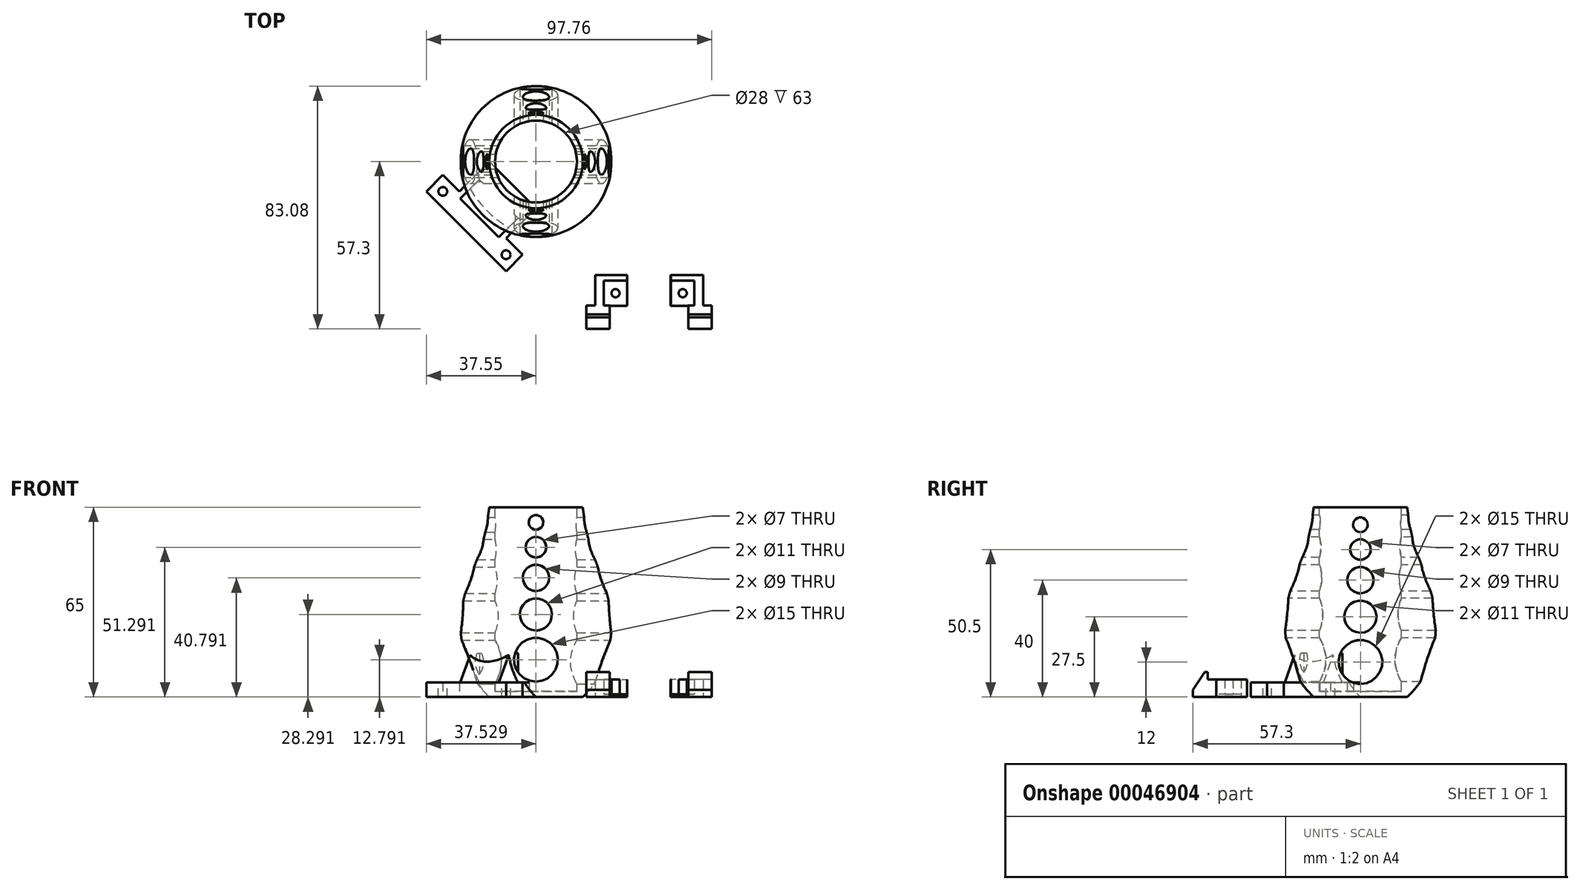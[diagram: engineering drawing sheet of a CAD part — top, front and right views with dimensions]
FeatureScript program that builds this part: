
annotation { "Feature Type Name" : "Feature", "Feature Type Description" : "" }
export const myFeature = defineFeature(function(context is Context, id is Id, definition is map)
    precondition{}
    {
        {
            var Q0;
            Q0=qCreatedBy(makeId("Front.planeOp"),FACE);
            var sketch = newSketch(context, id + "F0", { "sketchPlane" : qUnion([Q0])});
            skLineSegment(sketch, "E0", {"start": v(0, 0) * mm, "end": v(-16, 0) * mm});
            skLineSegment(sketch, "E1", {"start": v(0, 0) * mm, "end": v(0, 65) * mm, "construction": true});
            skLineSegment(sketch, "E2", {"start": v(0, 65) * mm, "end": v(-16, 65) * mm, "construction": true});
            skFitSpline(sketch, "E3", {"points": [v(-16, 0) * mm, v(-21.83, 7.5) * mm, v(-25.67, 28.22) * mm, v(-18.76, 51.24) * mm, v(-16, 65) * mm], "startDerivative": vector(-32.37, 32.77) * mm, "endDerivative": vector(7.4, 56.5) * mm});
            skLineSegment(sketch, "E4", {"start": v(-16, 65) * mm, "end": v(0, 65) * mm});
            skLineSegment(sketch, "E5", {"start": v(0, 65) * mm, "end": v(0, 0) * mm});
            skSolve(sketch);
        }
        {
            var Q0;
            Q0 = qSketchRegion(id + "F0", true);
            var Q1;
            Q1=sQuery(id+"F0.wireOp",EDGE,"E5");
            revolve(context, id + "F1", {"entities" : qUnion([Q0]), "axis" : qUnion([Q1]), "revolveType" : RevolveType.FULL});
        }
        {
            var Q0;
            Q0=makeQuery(id+"F1.opRevolve","SWEPT_FACE",FACE,{"disambiguationData":[OSD([sQuery(id+"F0.wireOp",EDGE,"E4")])]});
            var sketch = newSketch(context, id + "F2", { "sketchPlane" : qUnion([Q0])});
            skCircle(sketch, "E6", {"center": v(0, 0) * mm, "radius": 14 * mm});
            skCircle(sketch, "E7", {"center": v(0, 0) * mm, "radius": 15.98 * mm, "construction": true});
            skLineSegment(sketch, "E8", {"start": v(16, 0) * mm, "end": v(14, 0) * mm, "construction": true});
            skSolve(sketch);
        }
        {
            var Q0;
            Q0 = qSketchRegion(id + "F2", true);
            extrude(context, id + "F3", {"entities" : qUnion([Q0]), "operationType" : NewBodyOperationType.REMOVE, "oppositeDirection" : true, "depth" : 63 * mm});
        }
        {
            var Q0;
            Q0=qCreatedBy(makeId("Right.planeOp"),FACE);
            var sketch = newSketch(context, id + "F4", { "sketchPlane" : qUnion([Q0])});
            skLineSegment(sketch, "E9", {"start": v(0, 0) * mm, "end": v(0, 65) * mm, "construction": true});
            skCircle(sketch, "E10", {"center": v(0, 12) * mm, "radius": 7.5 * mm});
            skLineSegment(sketch, "E11", {"start": v(0, 19.5) * mm, "end": v(0, 27.5) * mm, "construction": true});
            skCircle(sketch, "E12", {"center": v(0, 27.5) * mm, "radius": 5.5 * mm});
            skLineSegment(sketch, "E13", {"start": v(0, 33) * mm, "end": v(0, 40) * mm, "construction": true});
            skCircle(sketch, "E14", {"center": v(0, 40) * mm, "radius": 4.5 * mm});
            skLineSegment(sketch, "E15", {"start": v(0, 44.5) * mm, "end": v(0, 50.5) * mm, "construction": true});
            skCircle(sketch, "E16", {"center": v(0, 50.5) * mm, "radius": 3.5 * mm});
            skLineSegment(sketch, "E17", {"start": v(0, 54) * mm, "end": v(0, 59) * mm, "construction": true});
            skCircle(sketch, "E18", {"center": v(0, 59) * mm, "radius": 2.5 * mm});
            skSolve(sketch);
        }
        {
            var Q0;
            Q0 = qSketchRegion(id + "F4", true);
            extrude(context, id + "F5", {"entities" : qUnion([Q0]), "operationType" : NewBodyOperationType.REMOVE, "endBound" : BoundingType.SYMMETRIC, "oppositeDirection" : true, "depth" : 60 * mm});
        }
        {
            var Q0;
            Q0=qCreatedBy(makeId("Front.planeOp"),FACE);
            var sketch = newSketch(context, id + "F6", { "sketchPlane" : qUnion([Q0])});
            skLineSegment(sketch, "E19", {"start": v(-0.02, 0.04) * mm, "end": v(-0.02, 65.04) * mm, "construction": true});
            skCircle(sketch, "E20", {"center": v(-0.02, 12.8) * mm, "radius": 7.5 * mm});
            skLineSegment(sketch, "E21", {"start": v(-0.02, 33.8) * mm, "end": v(-0.02, 40.8) * mm, "construction": true});
            skLineSegment(sketch, "E22", {"start": v(-0.02, 45.3) * mm, "end": v(-0.02, 51.3) * mm, "construction": true});
            skLineSegment(sketch, "E23", {"start": v(-0.02, 20.3) * mm, "end": v(-0.02, 28.3) * mm, "construction": true});
            skCircle(sketch, "E24", {"center": v(-0.02, 40.8) * mm, "radius": 4.5 * mm});
            skCircle(sketch, "E25", {"center": v(-0.02, 28.3) * mm, "radius": 5.5 * mm});
            skCircle(sketch, "E26", {"center": v(-0.02, 59.8) * mm, "radius": 2.5 * mm});
            skCircle(sketch, "E27", {"center": v(-0.02, 51.3) * mm, "radius": 3.5 * mm});
            skLineSegment(sketch, "E28", {"start": v(-0.02, 54.8) * mm, "end": v(-0.02, 59.8) * mm, "construction": true});
            skSolve(sketch);
        }
        {
            var Q0;
            Q0 = qSketchRegion(id + "F6", true);
            var Q1;
            Q1=sQuery(id+"F6.wireOp",EDGE,"E20");
            var Q2;
            Q2=sQuery(id+"F6.wireOp",EDGE,"E24");
            var Q3;
            Q3=sQuery(id+"F6.wireOp",EDGE,"E25");
            var Q4;
            Q4=sQuery(id+"F6.wireOp",EDGE,"E26");
            var Q5;
            Q5=sQuery(id+"F6.wireOp",EDGE,"E27");
            extrude(context, id + "F7", {"entities" : qUnion([Q0]), "operationType" : NewBodyOperationType.REMOVE, "surfaceEntities" : qUnion([Q1, Q2, Q3, Q4, Q5]), "endBound" : BoundingType.SYMMETRIC, "oppositeDirection" : true, "depth" : 60 * mm});
        }
        {
            var Q0;
            Q0=makeQuery(id+"F1.opRevolve","SWEPT_FACE",FACE,{"disambiguationData":[OSD([sQuery(id+"F0.wireOp",EDGE,"E0")])]});
            var sketch = newSketch(context, id + "F8", { "sketchPlane" : qUnion([Q0])});
            skLineSegment(sketch, "E29", {"start": v(0, 0) * mm, "end": v(-16, 0) * mm, "construction": true});
            skLineSegment(sketch, "E30", {"start": v(-16, 0) * mm, "end": v(0, 16) * mm, "construction": true});
            skLineSegment(sketch, "E31", {"start": v(0, 16) * mm, "end": v(0, 0) * mm, "construction": true});
            skLineSegment(sketch, "E32", {"start": v(0, 0) * mm, "end": v(-42.43, 42.43) * mm, "construction": true});
            skPoint(sketch, "E33.rect.middle", {"position": v(-8, 8) * mm});
            skLineSegment(sketch, "E34.rect.bottom", {"start": v(-38.93, 38.93) * mm, "end": v(-45.93, 38.93) * mm, "construction": true});
            skLineSegment(sketch, "E34.rect.top", {"start": v(-38.93, 45.93) * mm, "end": v(-45.93, 45.93) * mm, "construction": true});
            skLineSegment(sketch, "E34.rect.left", {"start": v(-38.93, 38.93) * mm, "end": v(-38.93, 45.93) * mm, "construction": true});
            skLineSegment(sketch, "E34.rect.right", {"start": v(-45.93, 38.93) * mm, "end": v(-45.93, 45.93) * mm, "construction": true});
            skPoint(sketch, "E34.rect.middle", {"position": v(-42.43, 42.43) * mm});
            skLineSegment(sketch, "E35", {"start": v(-45.93, 38.93) * mm, "end": v(-38.93, 45.93) * mm});
            skLineSegment(sketch, "E36", {"start": v(-11.5, 4.5) * mm, "end": v(-4.5, 11.5) * mm});
            skLineSegment(sketch, "E37", {"start": v(0, 16) * mm, "end": v(-16, 0) * mm});
            skLineSegment(sketch, "E38", {"start": v(-11.5, 4.5) * mm, "end": v(-25.64, 18.64) * mm, "construction": true});
            skPoint(sketch, "E39", {"position": v(-10.23, 37.55) * mm});
            skPoint(sketch, "E40", {"position": v(-25.64, 18.64) * mm});
            skLineSegment(sketch, "E41", {"start": v(-10.23, 37.55) * mm, "end": v(-37.55, 10.23) * mm, "construction": true});
            skLineSegment(sketch, "E42", {"start": v(-8, 8) * mm, "end": v(-18.23, 18.23) * mm, "construction": true});
            skLineSegment(sketch, "E43", {"start": v(-10.23, 37.55) * mm, "end": v(4.13, 23.18) * mm, "construction": true});
            skLineSegment(sketch, "E44", {"start": v(-37.55, 10.23) * mm, "end": v(-21.43, -5.88) * mm, "construction": true});
            skLineSegment(sketch, "E45", {"start": v(-31.9, 4.58) * mm, "end": v(-37.55, 10.23) * mm});
            skLineSegment(sketch, "E46", {"start": v(-37.55, 10.23) * mm, "end": v(-10.23, 37.55) * mm});
            skLineSegment(sketch, "E47", {"start": v(-4.58, 31.9) * mm, "end": v(-10.23, 37.55) * mm});
            skLineSegment(sketch, "E48", {"start": v(-16, 0) * mm, "end": v(-26.23, 10.23) * mm});
            skLineSegment(sketch, "E49", {"start": v(-26.23, 10.23) * mm, "end": v(-31.9, 4.58) * mm});
            skLineSegment(sketch, "E50", {"start": v(0, 16) * mm, "end": v(-10.23, 26.23) * mm});
            skLineSegment(sketch, "E51", {"start": v(-10.23, 26.23) * mm, "end": v(-4.58, 31.9) * mm});
            skSolve(sketch);
        }
        {
            var Q0;
            Q0 = qSketchRegion(id + "F8", true);
            extrude(context, id + "F9", {"entities" : qUnion([Q0]), "operationType" : NewBodyOperationType.ADD, "oppositeDirection" : true, "depth" : 5 * mm});
        }
        {
            var Q0;
            {var subQ0=sQuery(id+"F8.wireOp",EDGE,"E45");var subQ1=sQuery(id+"F8.wireOp",EDGE,"E46");var subQ2=sQuery(id+"F8.wireOp",EDGE,"E47");var subQ3=sQuery(id+"F8.wireOp",EDGE,"E48");var subQ4=sQuery(id+"F8.wireOp",EDGE,"E49");var subQ5=sQuery(id+"F8.wireOp",EDGE,"E50");var subQ6=sQuery(id+"F8.wireOp",EDGE,"E51");Q0=makeQuery(id+"F9.boolean.opBoolean","SPLIT",FACE,{"disambiguationData":[TD([makeQuery(id+"F1.opRevolve","SWEPT_FACE",FACE,{"disambiguationData":[OSD([sQuery(id+"F0.wireOp",EDGE,"E3")])]})])],"derivedFrom":makeQuery(id+"F9.opExtrude","CAP_FACE",FACE,{"disambiguationData":[OSD([sQuery(id+"F8.wireOp",EDGE,"E37"),subQ0,subQ1,subQ2,subQ3,subQ4,subQ5,subQ6])],"isStart":false})});}
            var sketch = newSketch(context, id + "F10", { "sketchPlane" : qUnion([Q0])});
            skLineSegment(sketch, "E52", {"start": v(-31.9, -4.58) * mm, "end": v(-26.23, -10.23) * mm, "construction": true});
            skLineSegment(sketch, "E53", {"start": v(-26.23, -10.23) * mm, "end": v(-31.9, -15.9) * mm, "construction": true});
            skLineSegment(sketch, "E54", {"start": v(-31.9, -15.9) * mm, "end": v(-31.9, -4.58) * mm, "construction": true});
            skLineSegment(sketch, "E55", {"start": v(-26.23, -10.23) * mm, "end": v(-37.55, -10.23) * mm, "construction": true});
            skLineSegment(sketch, "E56", {"start": v(-10.23, -26.23) * mm, "end": v(-15.9, -31.9) * mm, "construction": true});
            skLineSegment(sketch, "E57", {"start": v(-15.9, -31.9) * mm, "end": v(-4.58, -31.9) * mm, "construction": true});
            skLineSegment(sketch, "E58", {"start": v(-4.58, -31.9) * mm, "end": v(-10.23, -37.55) * mm, "construction": true});
            skLineSegment(sketch, "E59", {"start": v(-10.23, -37.55) * mm, "end": v(-10.23, -26.23) * mm, "construction": true});
            skCircle(sketch, "E60", {"center": v(-31.9, -10.23) * mm, "radius": 1.5 * mm});
            skCircle(sketch, "E61", {"center": v(-10.23, -31.9) * mm, "radius": 1.5 * mm});
            skSolve(sketch);
        }
        {
            var Q0;
            Q0 = qSketchRegion(id + "F10", true);
            extrude(context, id + "F11", {"entities" : qUnion([Q0]), "operationType" : NewBodyOperationType.REMOVE, "oppositeDirection" : true, "depth" : 6 * mm});
        }
        {
            var Q0;
            Q0=qCreatedBy(makeId("Top.planeOp"),FACE);
            var sketch = newSketch(context, id + "F12", { "sketchPlane" : qUnion([Q0])});
            skLineSegment(sketch, "E62", {"start": v(28.24, -40.8) * mm, "end": v(23.24, -40.8) * mm, "construction": true});
            skLineSegment(sketch, "E63", {"start": v(23.24, -40.8) * mm, "end": v(23.24, -49.3) * mm});
            skLineSegment(sketch, "E64", {"start": v(20.24, -38.8) * mm, "end": v(20.24, -49.3) * mm});
            skLineSegment(sketch, "E65", {"start": v(17.24, -49.3) * mm, "end": v(17.24, -52.3) * mm});
            skLineSegment(sketch, "E66", {"start": v(25.24, -49.3) * mm, "end": v(25.24, -52.3) * mm});
            skLineSegment(sketch, "E67", {"start": v(17.24, -52.3) * mm, "end": v(25.24, -52.3) * mm});
            skLineSegment(sketch, "E68.bottom", {"start": v(23.24, -40.8) * mm, "end": v(28.24, -40.8) * mm, "construction": true});
            skLineSegment(sketch, "E68.top", {"start": v(23.24, -49.3) * mm, "end": v(28.24, -49.3) * mm, "construction": true});
            skLineSegment(sketch, "E68.left", {"start": v(23.24, -40.8) * mm, "end": v(23.24, -49.3) * mm, "construction": true});
            skLineSegment(sketch, "E68.right", {"start": v(28.24, -40.8) * mm, "end": v(28.24, -49.3) * mm, "construction": true});
            skLineSegment(sketch, "E69", {"start": v(17.24, -49.3) * mm, "end": v(20.24, -49.3) * mm});
            skLineSegment(sketch, "E70", {"start": v(25.24, -49.3) * mm, "end": v(23.24, -49.3) * mm});
            skLineSegment(sketch, "E71", {"start": v(23.24, -40.8) * mm, "end": v(31.24, -40.8) * mm});
            skLineSegment(sketch, "E72", {"start": v(20.24, -38.8) * mm, "end": v(31.24, -38.8) * mm});
            skLineSegment(sketch, "E73", {"start": v(31.24, -38.8) * mm, "end": v(31.24, -40.8) * mm});
            skSolve(sketch);
        }
        {
            var Q0;
            {var subQ0=sQuery(id+"F8.wireOp",EDGE,"E45");var subQ1=sQuery(id+"F8.wireOp",EDGE,"E46");var subQ2=sQuery(id+"F8.wireOp",EDGE,"E47");var subQ3=sQuery(id+"F8.wireOp",EDGE,"E48");var subQ4=sQuery(id+"F8.wireOp",EDGE,"E49");var subQ5=sQuery(id+"F8.wireOp",EDGE,"E50");var subQ6=sQuery(id+"F8.wireOp",EDGE,"E51");Q0=makeQuery(id+"F9.boolean.opBoolean","SPLIT",FACE,{"disambiguationData":[TD([makeQuery(id+"F1.opRevolve","SWEPT_FACE",FACE,{"disambiguationData":[OSD([sQuery(id+"F0.wireOp",EDGE,"E3")])]})])],"derivedFrom":makeQuery(id+"F9.opExtrude","CAP_FACE",FACE,{"disambiguationData":[OSD([sQuery(id+"F8.wireOp",EDGE,"E37"),subQ0,subQ1,subQ2,subQ3,subQ4,subQ5,subQ6])],"isStart":false})});}
            var sketch = newSketch(context, id + "F13", { "sketchPlane" : qUnion([Q0])});
            skLineSegment(sketch, "E74", {"start": v(-19.95, -3.95) * mm, "end": v(-10.23, -37.55) * mm, "construction": true});
            skLineSegment(sketch, "E75", {"start": v(-3.95, -19.95) * mm, "end": v(-37.55, -10.23) * mm, "construction": true});
            skLineSegment(sketch, "E76", {"start": v(-16.36, -16.36) * mm, "end": v(-23.9, -23.9) * mm, "construction": true});
            skLineSegment(sketch, "E77", {"start": v(-31.9, -10.23) * mm, "end": v(-10.23, -31.9) * mm, "construction": true});
            skLineSegment(sketch, "E78", {"start": v(-26.23, -10.23) * mm, "end": v(-10.23, -26.23) * mm, "construction": true});
            skLineSegment(sketch, "E79", {"start": v(-9.12, -30.89) * mm, "end": v(-30.83, -9.17) * mm, "construction": true});
            skLineSegment(sketch, "E80", {"start": v(-26.6, -13.4) * mm, "end": v(-13.4, -26.61) * mm});
            skLineSegment(sketch, "E81", {"start": v(-13.4, -26.61) * mm, "end": v(-6.16, -19.38) * mm});
            skLineSegment(sketch, "E82", {"start": v(-26.6, -13.4) * mm, "end": v(-19.38, -6.16) * mm});
            skLineSegment(sketch, "E83", {"start": v(-19.38, -6.16) * mm, "end": v(-6.16, -19.38) * mm});
            skSolve(sketch);
        }
        {
            var Q0;
            Q0 = qSketchRegion(id + "F13", true);
            extrude(context, id + "F14", {"entities" : qUnion([Q0]), "operationType" : NewBodyOperationType.ADD, "depth" : 10 * mm});
        }
        {
            var Q0;
            Q0=makeQuery(id+"F14.opExtrude","CAP_EDGE",EDGE,{"disambiguationData":[OSD([sQuery(id+"F13.wireOp",EDGE,"E80")])],"isStart":false});
            chamfer(context, id + "F15", {"entities" : qUnion([Q0]), "chamferType" : ChamferType.TWO_OFFSETS, "width1" : 6 * mm, "oppositeDirection" : false, "width2" : 12 * mm, "tangentPropagation" : true});
        }
        {
            var Q0;
            Q0 = qSketchRegion(id + "F12", true);
            extrude(context, id + "F16", {"entities" : qUnion([Q0]), "depth" : 6 * mm});
        }
        {
            var Q0;
            Q0=qCreatedBy(makeId("Top.planeOp"),FACE);
            var sketch = newSketch(context, id + "F17", { "sketchPlane" : qUnion([Q0])});
            skLineSegment(sketch, "E84.bottom", {"start": v(31.22, -40.3) * mm, "end": v(22.77, -40.3) * mm});
            skLineSegment(sketch, "E84.top", {"start": v(31.22, -49.33) * mm, "end": v(22.77, -49.33) * mm});
            skLineSegment(sketch, "E84.left", {"start": v(31.22, -40.3) * mm, "end": v(31.22, -49.33) * mm});
            skLineSegment(sketch, "E84.right", {"start": v(22.77, -40.3) * mm, "end": v(22.77, -49.33) * mm});
            skSolve(sketch);
        }
        {
            var Q0;
            Q0 = qSketchRegion(id + "F17", true);
            extrude(context, id + "F18", {"entities" : qUnion([Q0]), "operationType" : NewBodyOperationType.ADD, "depth" : 1 * mm});
        }
        {
            var Q0;
            Q0=makeQuery(id+"F18.opExtrude","CAP_FACE",FACE,{"disambiguationData":[OSD([sQuery(id+"F17.wireOp",EDGE,"E84.bottom"),sQuery(id+"F17.wireOp",EDGE,"E84.top"),sQuery(id+"F17.wireOp",EDGE,"E84.left"),sQuery(id+"F17.wireOp",EDGE,"E84.right")])],"isStart":false});
            var sketch = newSketch(context, id + "F19", { "sketchPlane" : qUnion([Q0])});
            skLineSegment(sketch, "E85", {"start": v(31.22, -40.8) * mm, "end": v(23.24, -49.3) * mm, "construction": true});
            skLineSegment(sketch, "E86", {"start": v(23.24, -49.3) * mm, "end": v(23.24, -40.8) * mm, "construction": true});
            skLineSegment(sketch, "E87", {"start": v(23.24, -40.8) * mm, "end": v(31.22, -49.33) * mm, "construction": true});
            skPoint(sketch, "E88", {"position": v(27.22, -45.06) * mm});
            skCircle(sketch, "E89", {"center": v(27.22, -45.06) * mm, "radius": 1.4 * mm});
            skSolve(sketch);
        }
        {
            var Q0;
            Q0 = qSketchRegion(id + "F19", true);
            extrude(context, id + "F20", {"entities" : qUnion([Q0]), "operationType" : NewBodyOperationType.ADD, "depth" : 5 * mm});
        }
        {
            var Q0;
            Q0=makeQuery(id+"F16.opExtrude","SWEPT_FACE",FACE,{"disambiguationData":[OSD([sQuery(id+"F12.wireOp",EDGE,"E67")])]});
            var sketch = newSketch(context, id + "F21", { "sketchPlane" : qUnion([Q0])});
            skLineSegment(sketch, "E90.bottom", {"start": v(17.24, 0) * mm, "end": v(25.24, 0) * mm});
            skLineSegment(sketch, "E90.top", {"start": v(17.24, 8.5) * mm, "end": v(25.24, 8.5) * mm});
            skLineSegment(sketch, "E90.left", {"start": v(17.24, 0) * mm, "end": v(17.24, 8.5) * mm});
            skLineSegment(sketch, "E90.right", {"start": v(25.24, 0) * mm, "end": v(25.24, 8.5) * mm});
            skSolve(sketch);
        }
        {
            var Q0;
            Q0 = qSketchRegion(id + "F21", true);
            extrude(context, id + "F22", {"entities" : qUnion([Q0]), "operationType" : NewBodyOperationType.ADD, "depth" : 5 * mm});
        }
        {
            var Q0;
            Q0=makeQuery(id+"F22.opExtrude","CAP_EDGE",EDGE,{"disambiguationData":[OSD([sQuery(id+"F21.wireOp",EDGE,"E90.top")])],"isStart":false});
            chamfer(context, id + "F23", {"entities" : qUnion([Q0]), "chamferType" : ChamferType.TWO_OFFSETS, "width1" : 4 * mm, "oppositeDirection" : false, "width2" : 6 * mm, "tangentPropagation" : true});
        }
        {
            var Q0;
            Q0=makeQuery(id+"F16.opExtrude","SWEPT_BODY",BODY,{"disambiguationData":[OSD([sQuery(id+"F12.wireOp",EDGE,"E63"),sQuery(id+"F12.wireOp",EDGE,"E64"),sQuery(id+"F12.wireOp",EDGE,"E65"),sQuery(id+"F12.wireOp",EDGE,"E66"),sQuery(id+"F12.wireOp",EDGE,"E67"),sQuery(id+"F12.wireOp",EDGE,"E69"),sQuery(id+"F12.wireOp",EDGE,"E70"),sQuery(id+"F12.wireOp",EDGE,"E71"),sQuery(id+"F12.wireOp",EDGE,"E72"),sQuery(id+"F12.wireOp",EDGE,"E73")])]});
            transform(context, id + "F24", {"entities" : qUnion([Q0]), "transformType" : TransformType.TRANSLATION_3D, "dx" : 15 * mm, "dy" : 0 * mm, "dz" : 0 * mm, "makeCopy" : true});
        }
        {
            var Q0;
            Q0=makeQuery(id+"F24.opPattern","COPY",BODY,{"derivedFrom":makeQuery(id+"F16.opExtrude","SWEPT_BODY",BODY,{"disambiguationData":[OSD([sQuery(id+"F12.wireOp",EDGE,"E63"),sQuery(id+"F12.wireOp",EDGE,"E64"),sQuery(id+"F12.wireOp",EDGE,"E65"),sQuery(id+"F12.wireOp",EDGE,"E66"),sQuery(id+"F12.wireOp",EDGE,"E67"),sQuery(id+"F12.wireOp",EDGE,"E69"),sQuery(id+"F12.wireOp",EDGE,"E70"),sQuery(id+"F12.wireOp",EDGE,"E71"),sQuery(id+"F12.wireOp",EDGE,"E72"),sQuery(id+"F12.wireOp",EDGE,"E73")])]}),"instanceName":"1"});
            var Q1;
            Q1=makeQuery(id+"F24.opPattern","COPY",FACE,{"derivedFrom":makeQuery(id+"F18.opExtrude","SWEPT_FACE",FACE,{"disambiguationData":[OSD([sQuery(id+"F17.wireOp",EDGE,"E84.left")])]}),"instanceName":"1"});
            mirror(context, id + "F25", {"operationType" : NewBodyOperationType.ADD, "entities" : qUnion([Q0]), "mirrorPlane" : qUnion([Q1])});
        }
        {
            var Q0;
            Q0=makeQuery(id+"F24.opPattern","COPY",FACE,{"derivedFrom":makeQuery(id+"F22.boolean.opBoolean","MERGE",FACE,{"derivedFrom":[makeQuery(id+"F16.opExtrude","SWEPT_FACE",FACE,{"disambiguationData":[OSD([sQuery(id+"F12.wireOp",EDGE,"E65")])]}),makeQuery(id+"F22.opExtrude","SWEPT_FACE",FACE,{"disambiguationData":[OSD([sQuery(id+"F21.wireOp",EDGE,"E90.left")])]})]}),"instanceName":"1"});
            var sketch = newSketch(context, id + "F26", { "sketchPlane" : qUnion([Q0])});
            skLineSegment(sketch, "E91.bottom", {"start": v(38.38, -1.83) * mm, "end": v(58.93, -1.83) * mm});
            skLineSegment(sketch, "E91.top", {"start": v(38.38, 10.4) * mm, "end": v(58.93, 10.4) * mm});
            skLineSegment(sketch, "E91.left", {"start": v(38.38, -1.83) * mm, "end": v(38.38, 10.4) * mm});
            skLineSegment(sketch, "E91.right", {"start": v(58.93, -1.83) * mm, "end": v(58.93, 10.4) * mm});
            skSolve(sketch);
        }
        {
            var Q0;
            Q0 = qSketchRegion(id + "F26", true);
            extrude(context, id + "F27", {"entities" : qUnion([Q0]), "operationType" : NewBodyOperationType.REMOVE, "oppositeDirection" : true, "depth" : 13.83 * mm});
        }
    });
